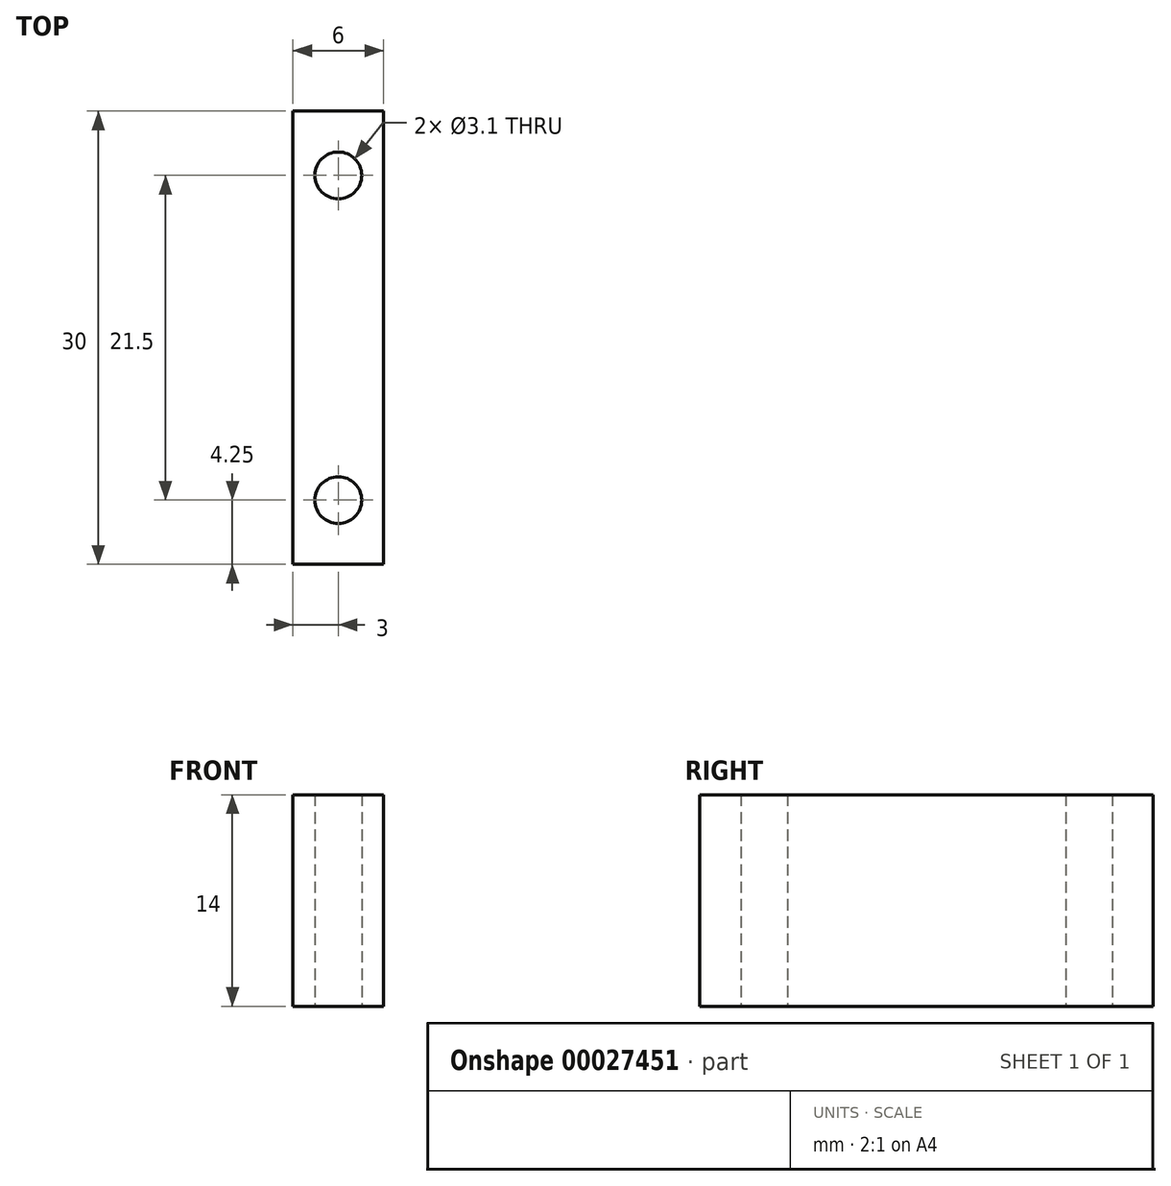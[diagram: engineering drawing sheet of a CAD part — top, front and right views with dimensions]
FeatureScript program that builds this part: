
annotation { "Feature Type Name" : "Feature", "Feature Type Description" : "" }
export const myFeature = defineFeature(function(context is Context, id is Id, definition is map)
    precondition{}
    {
        {
            var Q0;
            Q0=qCreatedBy(makeId("Top.planeOp"),FACE);
            var sketch = newSketch(context, id + "F0", { "sketchPlane" : qUnion([Q0])});
            skLineSegment(sketch, "E0.rect.bottom", {"start": v(-3, 15) * mm, "end": v(3, 15) * mm});
            skLineSegment(sketch, "E0.rect.top", {"start": v(-3, -15) * mm, "end": v(3, -15) * mm});
            skLineSegment(sketch, "E0.rect.left", {"start": v(-3, 15) * mm, "end": v(-3, -15) * mm});
            skLineSegment(sketch, "E0.rect.right", {"start": v(3, 15) * mm, "end": v(3, -15) * mm});
            skPoint(sketch, "E0.rect.middle", {"position": v(0, 0) * mm});
            skCircle(sketch, "E1", {"center": v(0, 10.75) * mm, "radius": 1.55 * mm});
            skCircle(sketch, "E2", {"center": v(0, -10.75) * mm, "radius": 1.55 * mm});
            skSolve(sketch);
        }
        {
            var Q0;
            Q0 = qSketchRegion(id + "F0", true);
            extrude(context, id + "F1", {"entities" : qUnion([Q0]), "depth" : 14 * mm});
        }
    });
